# Revit family: Pendant Lighting Fixture
name_source: partatom
category: Lighting Fixtures
revit_build: Autodesk Revit 2013 (Build: 20120221_2030(x64)
units: mm (PartAtom-declared; Revit-internal decimal feet)

## types (5) — shared parameters
Apparent Load = 0 VA
Color Filter = 16777215
Default Elevation = 4' - 0"
Dimming Lamp Color Temperature Shift = <None>
Emit Shape Visible in Rendering = No
Emit from Circle Diameter = 2' - 0"
Lamp = 1
Lamp Type = CFL
Lamp Wattage = 32 W
Load Clasification = Lighting
Number of Poles = 1
Photometric Web File = S4x46A12.ies
Power Factor = 1
Tilt Angle = -90.00°
Voltage = 277 V
Voltage Comment = 120/277

## per-type parameters (varying)
| type | Description | Fixture Height | Fixture Radius |
| 24" | 24" PENDANT LIGHT FIXTURE | 1' - 3" | 1' - 0" |
| 16" | 16" PENDANT LIGHT FIXTURE | 0' - 11" | 0' - 8" |
| 20" | 20" PENDANT LIGHT FIXTURE | 1' - 1" | 0' - 10" |
| 12" | 12" PENDANT LIGHT FIXTURE | 0' - 9" | 0' - 6" |
| 10" | 10" PENDANT LIGHT FIXTURE | 0' - 8" | 0' - 5" |

## geometry (parser evidence)
native form markers: Sweep x3
no freeform markers — native parametric forms only
